# Revit family: 2079900(n0300)
name_source: partatom
category: Security Devices
units: mm (PartAtom-declared; Revit-internal decimal feet)

## family parameters
Always vertical = No
Cut with Voids When Loaded = No
Host = Ceiling
OmniClass Number = 23.85.30.14
OmniClass Title = Presence Detection/Registration
Room Calculation Point = No
Shared = Yes

## types (2) — shared parameters
zero-valued in all types: A

## per-type parameters (varying)
- Type 1: CTN=0; EF000218=0 mm  [stored 0 ft]; EF000846=0 mm  [stored 0 ft]; EF001322=0 mm  [stored 0 ft]; EF001323=0 mm  [stored 0 ft]; EF003843=0 mm  [stored 0 ft]; EF003882=0; EF004265=0 mm  [stored 0 ft]; EF006589=0; EF006590=0; EF008011=0 mm  [stored 0 ft]; EF010517=0 mm  [stored 0 ft]; EF010886=0 mm  [stored 0 ft]; EF010945=0 mm  [stored 0 ft]; EF010946=0 mm  [stored 0 ft]; LOG=0; NOCUPEROU=0; PRICEQUANTITY=0; QUANTITYINT=0; QUANTITYMIN=0
- 2079900: ARTICLENO=NB; BOMINFO=LINA; CATALOG=Theben; COO=HU; CTN=90314990; DEEPLINK_PRODUKTSEITE=http://www.theben.de; DESCLONG=Multisensor KNX, consisting of KNX passive infrared presence detector and room air sensor (= 2 bus devices), Functions room air sensor: Measures CO2 concentration, relative humidity, temperature and air pressure, Three independent parameterizable thresholds for CO2 concentration and relative humidity, Integrated room temperature controller, 4 binary inputs, Functions presence detector: KNX presence detector for ceiling mounting, square detection area 360°, up to 10 x 10 m (100 m2), three channels light for control of three light groups, switching or constant light control, operation as full or semi-automatic switchable, channel brightness with cyclic output, channel for room monitoring, reduction of overrun time light for short presence, mixed light measurement, Light switch-off delay self-learning, switching between 2 brightness setpoints, brightness setpoints adjustable via bus, stand-by functionality, 2 presence channels with switch-on delay/inactive, switch-off delay adjustable, parameters can be remotely controlled and read out, master/slave operation selectable, test functions, scene control with two scenes, 8-bit scenes, integrated bus coupling unit; DESCSHORT=Multisensor KNX, consisting of KNX passive infrared presence detector and room air sensor; EF000003=EV000384; EF000007=White; EF000010=Presence detector; EF000139=Untreated; EF000147=false; EF000218=1 mm  [stored 0.00328084 ft]; EF000846=1 mm  [stored 0.00328084 ft]; EF001098=true; EF001257=Thermoplast; EF001322=5000 mm; EF001323=5000 mm; EF002169=Plastic; EF003843=10000 mm; EF003876=true; EF003882=9010; EF003898=true; EF004265=15 mm  [stored 0.0492126 ft]; EF006243=false; EF006311=false; EF006569=matt; EF006582=0, 360 °; EF006589=30; EF006590=60; EF007575=true; EF008011=3000 mm; EF010517=67 mm; EF010886=45 mm  [stored 0.147638 ft]; EF010945=134 mm; EF010946=55 mm  [stored 0.180446 ft]; GEBRAUCHSANLEITUNG=http://www.theben.de; INTNO=4003468200414; LINA=2079900; LOG=300; MANUID=2079900; MANUNAME=Theben AG; MANUTYPEDESC=thePrema P360 KNX AP Multi WH; Manufacturer=Theben; Model=2079900; NB=2079900(N0300); NBSYN=$MANUID.($SA.$A.$LOG.); NN=thePrema P KNX; NOCUPEROU=1; PRICEQUANTITY=1; PRODUKTDATENBLATT=http://www.theben.de; QUANTITYINT=1; QUANTITYMIN=1; REACH_ERKLAERUNG=http://www.theben.de; REMARKS=ERP-GROUP 360; SA=None; SUPPLIER=THEBEN; SUPPLIERALTNO=2079900

note: [stored X ft] marks values corroborated as IEEE doubles in the binary element streams (Revit-internal decimal feet)

## geometry (parser evidence)
native form markers: Sweep x13
no freeform markers — native parametric forms only
